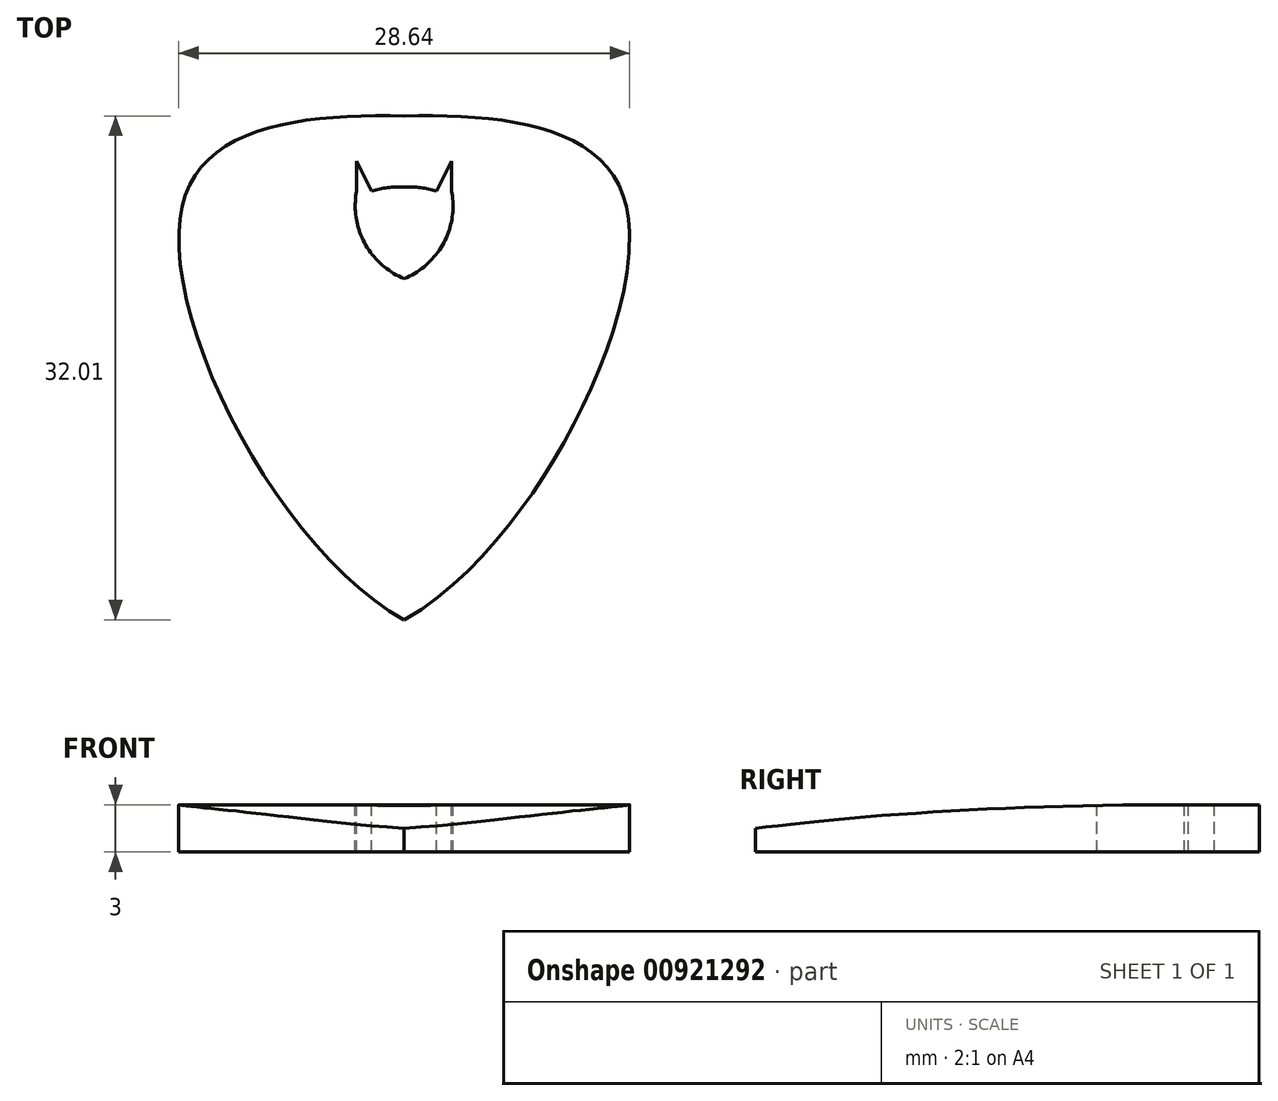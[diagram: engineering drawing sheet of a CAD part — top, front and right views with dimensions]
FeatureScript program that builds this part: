
annotation { "Feature Type Name" : "Feature", "Feature Type Description" : "" }
export const myFeature = defineFeature(function(context is Context, id is Id, definition is map)
    precondition{}
    {
        {
            var Q0;
            Q0=qCreatedBy(makeId("Top.planeOp"),FACE);
            var sketch = newSketch(context, id + "F0", { "sketchPlane" : qUnion([Q0])});
            skLineSegment(sketch, "E0", {"start": v(0, 0) * mm, "end": v(0, 16) * mm, "construction": true});
            skLineSegment(sketch, "E1.MirrorCS", {"start": v(0, 0) * mm, "end": v(0, -16) * mm, "construction": true});
            skLineSegment(sketch, "E2", {"start": v(0, 10.65) * mm, "end": v(-14, 10.65) * mm, "construction": true});
            skLineSegment(sketch, "E3.MirrorCS", {"start": v(0, 10.65) * mm, "end": v(14, 10.65) * mm, "construction": true});
            skFitSpline(sketch, "E4", {"points": [v(0, 16) * mm, v(-14, 10.65) * mm, v(0, -16) * mm], "startDerivative": vector(-44.9, 0.92) * mm, "endDerivative": vector(41.2, -22.68) * mm});
            skFitSpline(sketch, "E5.MirrorCS", {"points": [v(0, 16) * mm, v(14, 10.65) * mm, v(0, -16) * mm], "startDerivative": vector(44.9, 0.92) * mm, "endDerivative": vector(-41.2, -22.68) * mm});
            skSolve(sketch);
        }
        {
            var Q0;
            Q0=makeQuery(id+"F0.imprint","IMPRINT",FACE,{"disambiguationData":[TD([[makeQuery(id+"F0.imprint","IMPRINT",EDGE,{"derivedFrom":sQuery(id+"F0.wireOp",EDGE,"E4")}),1.0]])]});
            extrude(context, id + "F1", {"entities" : qUnion([Q0]), "endBound" : BoundingType.SYMMETRIC, "depth" : 3 * mm, "offsetDistance" : 25 * mm});
        }
        {
            var Q0;
            Q0=qCreatedBy(makeId("Right.planeOp"),FACE);
            cPlane(context, id + "F2", {"entities" : qUnion([Q0]), "cplaneType" : CPlaneType.OFFSET, "offset" : 15 * mm, "width" : 150 * mm, "height" : 150 * mm});
        }
        {
            var Q0;
            Q0=qCreatedBy(id+"F2.planeOp",FACE);
            var sketch = newSketch(context, id + "F3", { "sketchPlane" : qUnion([Q0])});
            skLineSegment(sketch, "E6.2", {"start": v(16, 1.5) * mm, "end": v(16, -1.5) * mm});
            skLineSegment(sketch, "E6.3", {"start": v(-16, 1.5) * mm, "end": v(-16, -1.5) * mm});
            skLineSegment(sketch, "E7", {"start": v(-16, 0) * mm, "end": v(16, 0) * mm, "construction": true});
            skFitSpline(sketch, "E8", {"points": [v(-16, 0) * mm, v(16, 1.5) * mm], "startDerivative": vector(32.65, 4.06) * mm, "endDerivative": vector(31.8, -0.27) * mm});
            skLineSegment(sketch, "E9", {"start": v(-16, -1.5) * mm, "end": v(16, -1.5) * mm});
            skLineSegment(sketch, "E10", {"start": v(-16, 1.5) * mm, "end": v(16, 1.5) * mm});
            skSolve(sketch);
        }
        {
            var Q0;
            {var subQ0=sQuery(id+"F3.wireOp",EDGE,"E10");var subQ1=sQuery(id+"F3.wireOp",EDGE,"E6.3");var subQ2=makeQuery(id+"F3.imprint","INTERSECT",VERTEX,{"derivedFrom":[subQ1,subQ0]});Q0=makeQuery(id+"F3.imprint","IMPRINT",FACE,{"disambiguationData":[TD([[makeQuery(id+"F3.imprint","IMPRINT",EDGE,{"disambiguationData":[TD([[subQ2,-1.0]])],"derivedFrom":subQ1}),1.0]])]});}
            extrude(context, id + "F4", {"entities" : qUnion([Q0]), "operationType" : NewBodyOperationType.REMOVE, "oppositeDirection" : true, "depth" : 35 * mm, "offsetDistance" : 25 * mm});
        }
        {
            var Q0;
            Q0=makeQuery(id+"F1.opExtrude","CAP_FACE",FACE,{"disambiguationData":[OSD([sQuery(id+"F0.wireOp",EDGE,"E4"),sQuery(id+"F0.wireOp",EDGE,"E5.MirrorCS")])],"isStart":false});
            var sketch = newSketch(context, id + "F5", { "sketchPlane" : qUnion([Q0])});
            skLineSegment(sketch, "E11", {"start": v(0, 16) * mm, "end": v(0, 0) * mm, "construction": true});
            skArc(sketch, "E12", {"start": v(0, 11.48) * mm, "mid": v(-1.05, 11.45) * mm, "end": v(-2.07, 11.24) * mm});
            skLineSegment(sketch, "E13", {"start": v(-2.07, 11.24) * mm, "end": v(-3.02, 13.14) * mm});
            skLineSegment(sketch, "E14", {"start": v(-3.02, 13.14) * mm, "end": v(-3.02, 11.24) * mm});
            skArc(sketch, "E15", {"start": v(-3.02, 11.24) * mm, "mid": v(-2.5, 7.92) * mm, "end": v(0, 5.67) * mm});
            skArc(sketch, "E16.MirrorCS", {"start": v(0, 11.48) * mm, "mid": v(1.05, 11.45) * mm, "end": v(2.07, 11.24) * mm});
            skLineSegment(sketch, "E17.MirrorCS", {"start": v(2.07, 11.24) * mm, "end": v(3.02, 13.14) * mm});
            skLineSegment(sketch, "E18.MirrorCS", {"start": v(3.02, 13.14) * mm, "end": v(3.02, 11.24) * mm});
            skArc(sketch, "E19.MirrorCS", {"start": v(3.02, 11.24) * mm, "mid": v(2.5, 7.92) * mm, "end": v(0, 5.67) * mm});
            skSolve(sketch);
        }
        {
            var Q0;
            Q0=makeQuery(id+"F5.imprint","IMPRINT",FACE,{"disambiguationData":[TD([[makeQuery(id+"F5.imprint","IMPRINT",EDGE,{"derivedFrom":sQuery(id+"F5.wireOp",EDGE,"E12")}),1.0]])]});
            var Q1;
            {var subQ0=sQuery(id+"F5.wireOp",EDGE,"E19.MirrorCS");var subQ1=sQuery(id+"F5.wireOp",EDGE,"E15");var subQ2=makeQuery(id+"F5.imprint","INTERSECT",VERTEX,{"derivedFrom":[subQ1,subQ0]});Q1=makeQuery(id+"F5.imprint","IMPRINT",FACE,{"disambiguationData":[TD([[makeQuery(id+"F5.imprint","IMPRINT",EDGE,{"disambiguationData":[TD([[subQ2,1.0]])],"derivedFrom":subQ1}),1.0]])]});}
            extrude(context, id + "F6", {"entities" : qUnion([Q0, Q1]), "operationType" : NewBodyOperationType.REMOVE, "oppositeDirection" : true, "depth" : 25 * mm, "offsetDistance" : 25 * mm});
        }
    });
